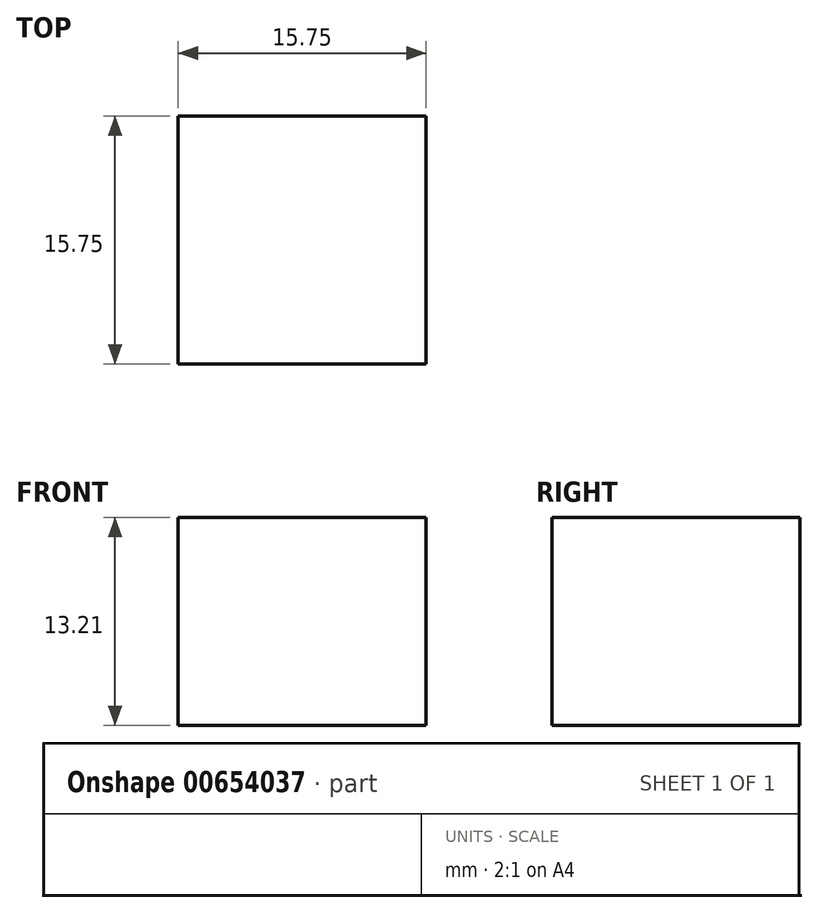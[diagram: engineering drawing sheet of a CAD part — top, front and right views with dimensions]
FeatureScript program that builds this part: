
annotation { "Feature Type Name" : "Feature", "Feature Type Description" : "" }
export const myFeature = defineFeature(function(context is Context, id is Id, definition is map)
    precondition{}
    {
        {
            var Q0;
            Q0=qCreatedBy(makeId("Top.planeOp"),FACE);
            var sketch = newSketch(context, id + "F0", { "sketchPlane" : qUnion([Q0])});
            skLineSegment(sketch, "E0.bottom", {"start": v(0, 0) * mm, "end": v(15.75, 0) * mm});
            skLineSegment(sketch, "E0.top", {"start": v(0, -15.75) * mm, "end": v(15.75, -15.75) * mm});
            skLineSegment(sketch, "E0.left", {"start": v(0, 0) * mm, "end": v(0, -15.75) * mm});
            skLineSegment(sketch, "E0.right", {"start": v(15.75, 0) * mm, "end": v(15.75, -15.75) * mm});
            skSolve(sketch);
        }
        {
            var Q0;
            Q0 = qSketchRegion(id + "F0", true);
            var Q1;
            Q1=makeQuery(id+"F0.imprint","IMPRINT",FACE,{"disambiguationData":[TD([[makeQuery(id+"F0.imprint","IMPRINT",EDGE,{"derivedFrom":sQuery(id+"F0.wireOp",EDGE,"E0.bottom")}),-1.0]])]});
            extrude(context, id + "F1", {"entities" : qUnion([Q0, Q1]), "depth" : 13.2 * mm, "offsetDistance" : 25.4 * mm});
        }
    });
